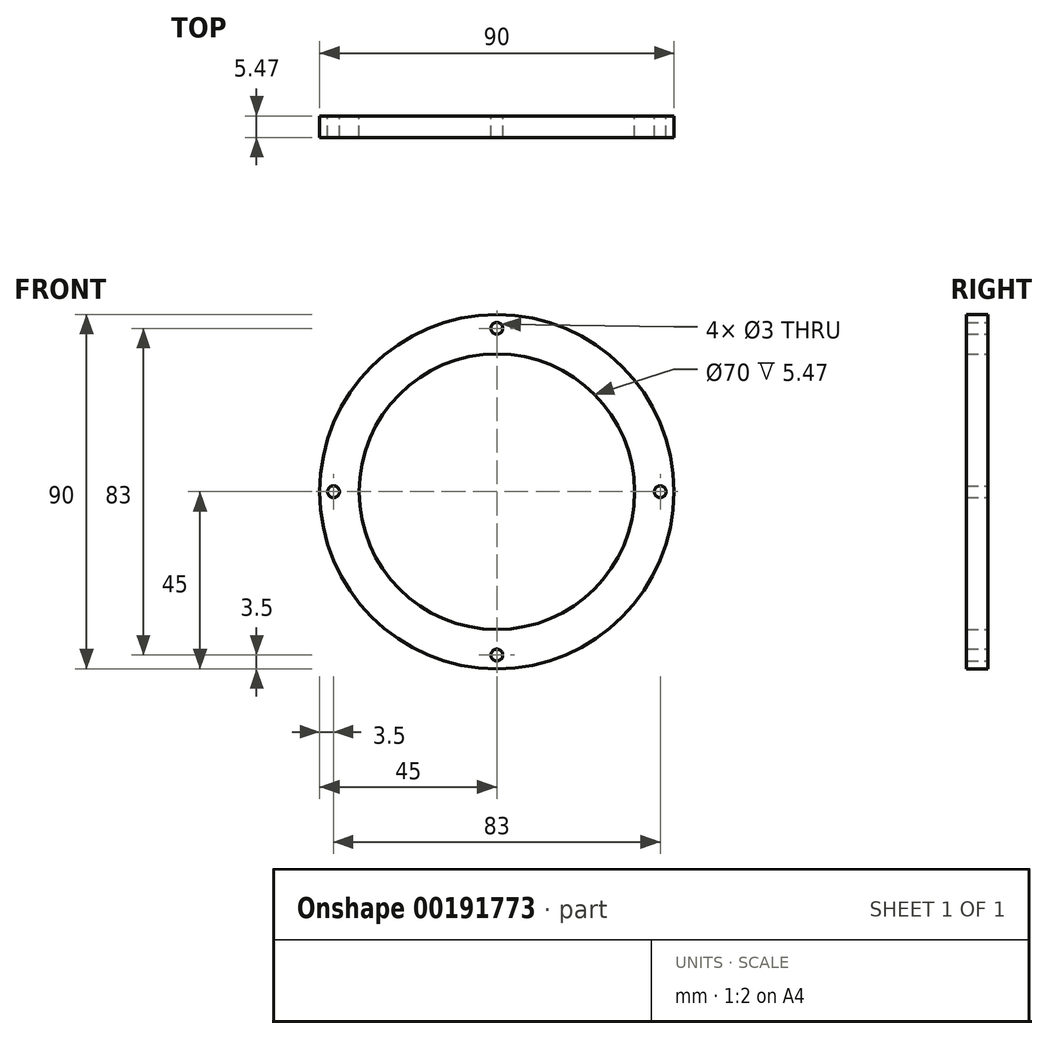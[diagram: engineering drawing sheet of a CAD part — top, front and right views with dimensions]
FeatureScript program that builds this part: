
annotation { "Feature Type Name" : "Feature", "Feature Type Description" : "" }
export const myFeature = defineFeature(function(context is Context, id is Id, definition is map)
    precondition{}
    {
        {
            var Q0;
            Q0=qCreatedBy(makeId("Front.planeOp"),FACE);
            var sketch = newSketch(context, id + "F0", { "sketchPlane" : qUnion([Q0])});
            skCircle(sketch, "E0", {"center": v(0, 0) * mm, "radius": 35 * mm});
            skCircle(sketch, "E1", {"center": v(0, 0) * mm, "radius": 45 * mm});
            skCircle(sketch, "E2", {"center": v(0, 0) * mm, "radius": 41.5 * mm, "construction": true});
            skCircle(sketch, "E3", {"center": v(0, 41.5) * mm, "radius": 1.5 * mm});
            skCircle(sketch, "E4.1.0", {"center": v(-41.5, 0) * mm, "radius": 1.5 * mm});
            skCircle(sketch, "E4.2.0", {"center": v(0, -41.5) * mm, "radius": 1.5 * mm});
            skCircle(sketch, "E4.3.0", {"center": v(41.5, 0) * mm, "radius": 1.5 * mm});
            skSolve(sketch);
        }
        {
            var Q0;
            Q0=makeQuery(id+"F0.imprint","IMPRINT",FACE,{"disambiguationData":[TD([[makeQuery(id+"F0.imprint","IMPRINT",EDGE,{"derivedFrom":sQuery(id+"F0.wireOp",EDGE,"E0")}),-1.0]])]});
            extrude(context, id + "F1", {"entities" : qUnion([Q0]), "depth" : 5.47 * mm});
        }
    });
